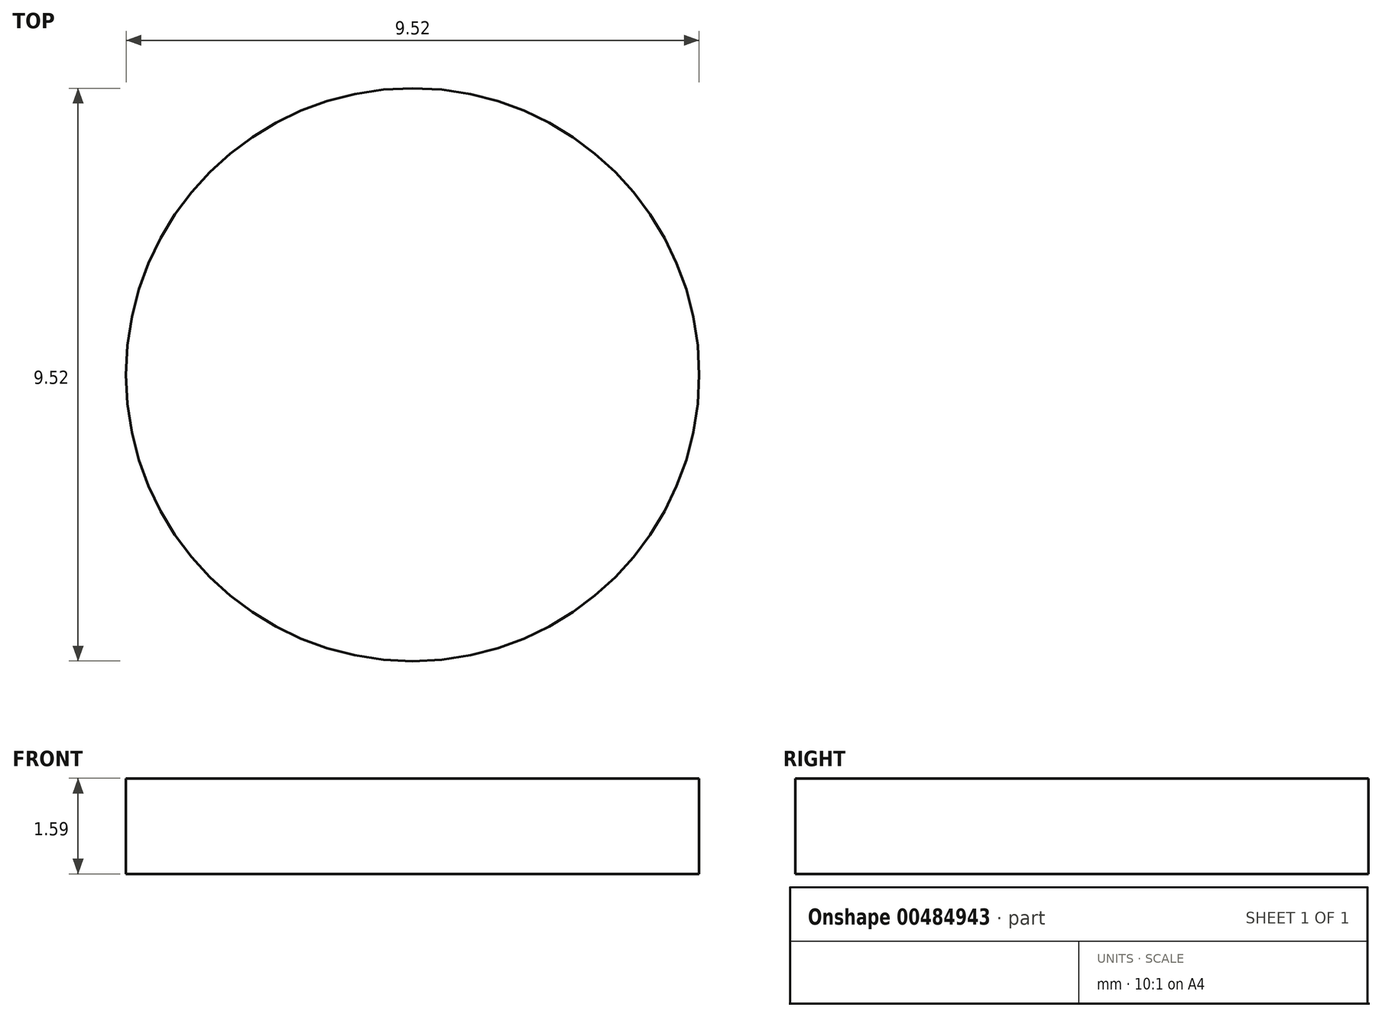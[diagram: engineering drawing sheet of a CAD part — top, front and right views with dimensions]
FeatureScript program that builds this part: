
annotation { "Feature Type Name" : "Feature", "Feature Type Description" : "" }
export const myFeature = defineFeature(function(context is Context, id is Id, definition is map)
    precondition{}
    {
        {
            var Q0;
            Q0=qCreatedBy(makeId("Top.planeOp"),FACE);
            var sketch = newSketch(context, id + "F0", { "sketchPlane" : qUnion([Q0])});
            skCircle(sketch, "E0", {"center": v(0, 0) * mm, "radius": 4.76 * mm});
            skSolve(sketch);
        }
        {
            var Q0;
            Q0 = qSketchRegion(id + "F0", true);
            extrude(context, id + "F1", {"entities" : qUnion([Q0]), "depth" : 1.59 * mm});
        }
    });
